# Revit family: PLFY-P50VFM-E
name_source: partatom
category: Mechanical Equipment
revit_build: Autodesk Revit Architecture 2012 (Build: 20110916_2132(x64)
units: mm (PartAtom-declared; Revit-internal decimal feet)

## types (1)
- PLFY-P50VFM-E
    Airflow Rate_High (m3/h) = 780
    Airflow Rate_High (m3/min) = 13
    Airflow Rate_Low (m3/h) = 540
    Airflow Rate_Low (m3/min) = 9
    Airflow Rate_Mid (m3/h) = 660
    Airflow Rate_Mid (m3/min) = 11
    Cooling Current (A) = 0.4
    Cooling Power Input (kW) = 0.04
    Depth = 570 mm  [stored 1.87008 ft]
    Description = Ceiling cassette
    Drain pipe_radius = 16 mm  [stored 0.0524934 ft]
    Equip_No. = 0
    External Finish = Munsell 6.4Y 8.9/0.4
    Fan Motor Output (kW) = 0.05
    Fan_Quantity = 1
    Fan_Type = Turbo fan
    Gas pipe_radius = 6 mm  [stored 0.019685 ft]
    Heating Current (A) = 0.35
    Heating Power Input (kW) = 0.04
    Height = 245 mm
    Hertz = 50 Hz
    Liquid pipe_radius = 3 mm  [stored 0.00984252 ft]
    Manufacturer = Mitsubishi Electric Corporation
    Model = PLFY-P50VFM-E
    Panel Weight (kg) = 3
    Panel depth = 625 mm
    Panel height = 10 mm  [stored 0.0328084 ft]
    Panel width = 625 mm
    Phase = 1
    SerialNumber = 0
    Sound Pressure Level_High (dB(A)) = 43
    Sound Pressure Level_Low (dB(A)) = 33
    Sound Pressure Level_Mid (dB(A)) = 39
    Space View = Yes
    Subcategory = HVAC
    TagNumber = 0
    URL = http://www.mitsubishielectric.com
    Unit Weight (kg) = 15
    Voltage = 230 V
    Width = 570 mm  [stored 1.87008 ft]

note: [stored X ft] marks values corroborated as IEEE doubles in the binary element streams (Revit-internal decimal feet)

## geometry (parser evidence)
native form markers: Blend x20, Sweep x10
no freeform markers — native parametric forms only
